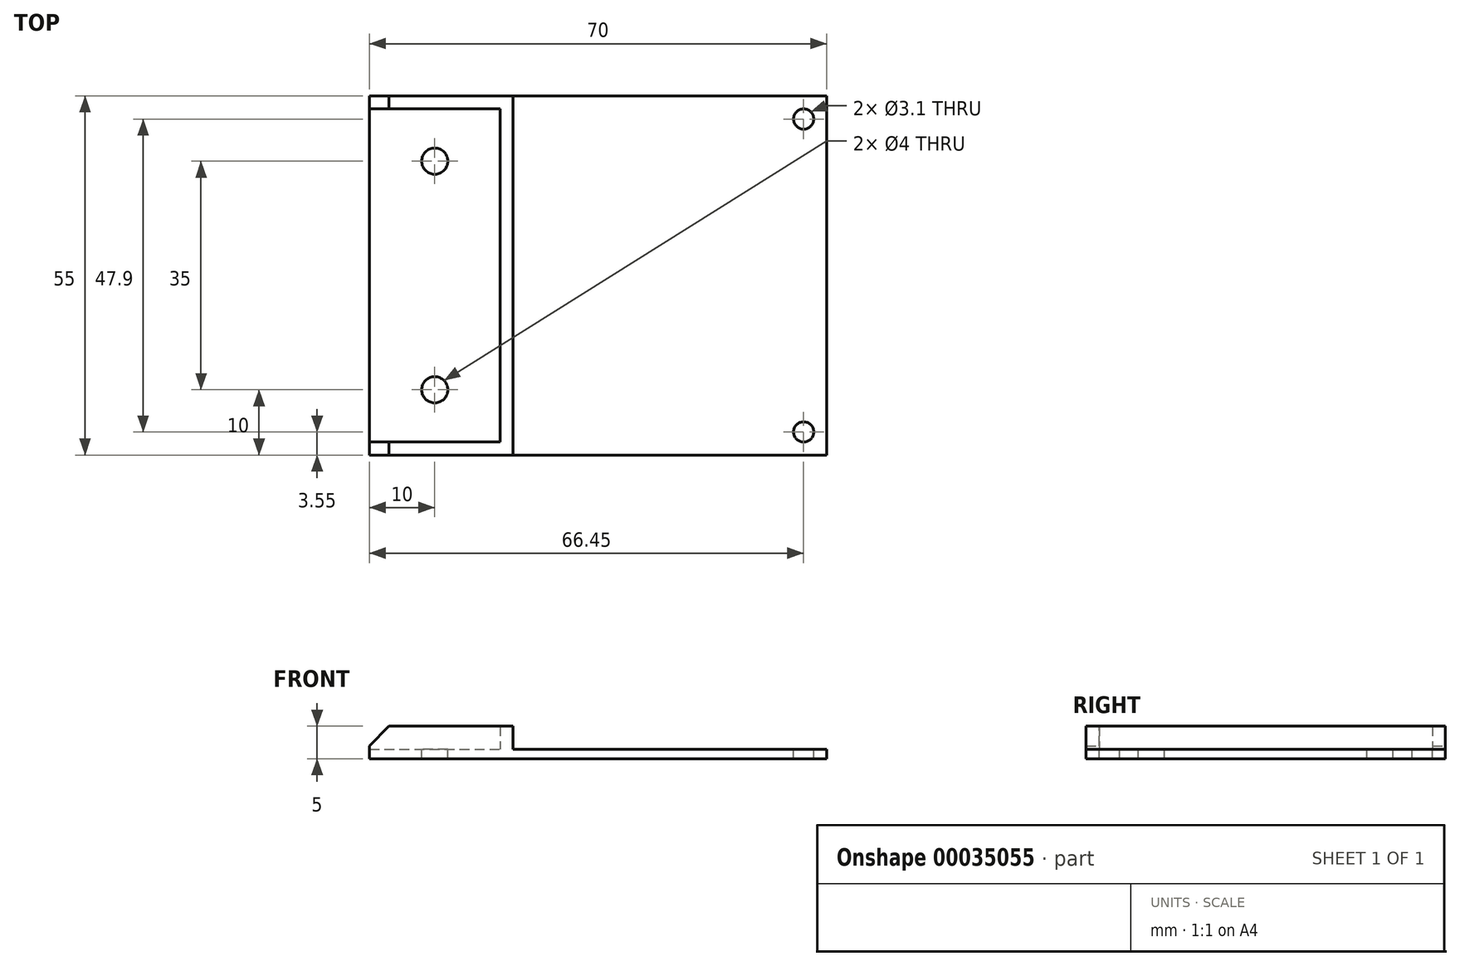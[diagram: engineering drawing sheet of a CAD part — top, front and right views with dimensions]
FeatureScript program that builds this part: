
annotation { "Feature Type Name" : "Feature", "Feature Type Description" : "" }
export const myFeature = defineFeature(function(context is Context, id is Id, definition is map)
    precondition{}
    {
        {
            var Q0;
            Q0=qCreatedBy(makeId("Top.planeOp"),FACE);
            var sketch = newSketch(context, id + "F0", { "sketchPlane" : qUnion([Q0])});
            skLineSegment(sketch, "E0.rect.bottom", {"start": v(35, -27.5) * mm, "end": v(-35, -27.5) * mm});
            skLineSegment(sketch, "E0.rect.top", {"start": v(35, 27.5) * mm, "end": v(-35, 27.5) * mm});
            skLineSegment(sketch, "E0.rect.left", {"start": v(35, -27.5) * mm, "end": v(35, 27.5) * mm});
            skLineSegment(sketch, "E0.rect.right", {"start": v(-35, -27.5) * mm, "end": v(-35, 27.5) * mm});
            skPoint(sketch, "E0.rect.middle", {"position": v(0, 0) * mm});
            skLineSegment(sketch, "E1", {"start": v(-25, 27.5) * mm, "end": v(-25, -27.5) * mm, "construction": true});
            skLineSegment(sketch, "E2", {"start": v(-35, 0) * mm, "end": v(35, 0) * mm, "construction": true});
            skLineSegment(sketch, "E3", {"start": v(35, 25.5) * mm, "end": v(-35, 25.5) * mm, "construction": true});
            skLineSegment(sketch, "E4", {"start": v(33, 27.5) * mm, "end": v(33, -27.5) * mm, "construction": true});
            skCircle(sketch, "E5", {"center": v(31.45, 23.95) * mm, "radius": 1.55 * mm});
            skCircle(sketch, "E6", {"center": v(-25, 17.5) * mm, "radius": 2 * mm});
            skCircle(sketch, "E7.MirrorC", {"center": v(-25, -17.5) * mm, "radius": 2 * mm});
            skCircle(sketch, "E8.MirrorC", {"center": v(31.45, -23.95) * mm, "radius": 1.55 * mm});
            skSolve(sketch);
        }
        {
            var Q0;
            Q0=makeQuery(id+"F0.imprint","IMPRINT",FACE,{"disambiguationData":[TD([[makeQuery(id+"F0.imprint","IMPRINT",EDGE,{"derivedFrom":sQuery(id+"F0.wireOp",EDGE,"E0.rect.bottom")}),-1.0]])]});
            extrude(context, id + "F1", {"entities" : qUnion([Q0]), "oppositeDirection" : true, "depth" : 1.5 * mm});
        }
        {
            var Q0;
            Q0=makeQuery(id+"F1.opExtrude","CAP_FACE",FACE,{"disambiguationData":[OSD([sQuery(id+"F0.wireOp",EDGE,"E0.rect.bottom"),sQuery(id+"F0.wireOp",EDGE,"E0.rect.top"),sQuery(id+"F0.wireOp",EDGE,"E0.rect.left"),sQuery(id+"F0.wireOp",EDGE,"E0.rect.right"),sQuery(id+"F0.wireOp",EDGE,"E5"),sQuery(id+"F0.wireOp",EDGE,"E6"),sQuery(id+"F0.wireOp",EDGE,"E7.MirrorC"),sQuery(id+"F0.wireOp",EDGE,"E8.MirrorC")])],"isStart":true});
            var sketch = newSketch(context, id + "F2", { "sketchPlane" : qUnion([Q0])});
            skLineSegment(sketch, "E9.top", {"start": v(-13, -25.5) * mm, "end": v(33, -25.5) * mm});
            skLineSegment(sketch, "E9.left", {"start": v(-13, 25.5) * mm, "end": v(-13, -25.5) * mm});
            skLineSegment(sketch, "E9.right", {"start": v(33, 26.5) * mm, "end": v(33, -25.5) * mm});
            skLineSegment(sketch, "E10.bottom", {"start": v(35, -27.5) * mm, "end": v(-15, -27.5) * mm});
            skLineSegment(sketch, "E10.top", {"start": v(35, 27.5) * mm, "end": v(-15, 27.5) * mm});
            skLineSegment(sketch, "E10.left", {"start": v(35, -27.5) * mm, "end": v(35, 27.5) * mm});
            skLineSegment(sketch, "E10.right", {"start": v(-15, -27.5) * mm, "end": v(-15, 27.5) * mm});
            skLineSegment(sketch, "E11.bottom", {"start": v(-35, 27.5) * mm, "end": v(-13, 27.5) * mm});
            skLineSegment(sketch, "E11.left", {"start": v(-35, 27.5) * mm, "end": v(-35, 25.5) * mm});
            skLineSegment(sketch, "E11.right", {"start": v(-13, 27.5) * mm, "end": v(-13, 25.5) * mm});
            skLineSegment(sketch, "E12.bottom", {"start": v(-13, -25.5) * mm, "end": v(-35, -25.5) * mm});
            skLineSegment(sketch, "E12.top", {"start": v(-13, -27.5) * mm, "end": v(-35, -27.5) * mm});
            skLineSegment(sketch, "E12.left", {"start": v(-13, -25.5) * mm, "end": v(-13, -27.5) * mm});
            skLineSegment(sketch, "E12.right", {"start": v(-35, -25.5) * mm, "end": v(-35, -27.5) * mm});
            skLineSegment(sketch, "E13", {"start": v(-35, 25.5) * mm, "end": v(33, 25.5) * mm});
            skSolve(sketch);
        }
        {
            var Q0;
            {var subQ3=sQuery(id+"F2.wireOp",EDGE,"E9.left");Q0=makeQuery(id+"F2.imprint","IMPRINT",FACE,{"disambiguationData":[TD([[makeQuery(id+"F2.imprint","IMPRINT",EDGE,{"derivedFrom":subQ3}),-1.0]])]});}
            var Q1;
            Q1=makeQuery(id+"F2.imprint","IMPRINT",FACE,{"disambiguationData":[TD([[makeQuery(id+"F2.imprint","IMPRINT",EDGE,{"derivedFrom":sQuery(id+"F2.wireOp",EDGE,"E10.bottom")}),-1.0]])]});
            var Q2;
            {var subQ0=sQuery(id+"F2.wireOp",EDGE,"E12.left");Q2=makeQuery(id+"F2.imprint","IMPRINT",FACE,{"disambiguationData":[TD([[makeQuery(id+"F2.imprint","IMPRINT",EDGE,{"derivedFrom":subQ0}),-1.0]])]});}
            var Q3;
            {var subQ0=sQuery(id+"F2.wireOp",EDGE,"E12.right");Q3=makeQuery(id+"F2.imprint","IMPRINT",FACE,{"disambiguationData":[TD([[makeQuery(id+"F2.imprint","IMPRINT",EDGE,{"derivedFrom":subQ0}),-1.0]])]});}
            var Q4;
            {var subQ0=sQuery(id+"F2.wireOp",EDGE,"E11.right");Q4=makeQuery(id+"F2.imprint","IMPRINT",FACE,{"disambiguationData":[TD([[makeQuery(id+"F2.imprint","IMPRINT",EDGE,{"derivedFrom":subQ0}),-1.0]])]});}
            var Q5;
            {var subQ0=sQuery(id+"F2.wireOp",EDGE,"E11.left");Q5=makeQuery(id+"F2.imprint","IMPRINT",FACE,{"disambiguationData":[TD([[makeQuery(id+"F2.imprint","IMPRINT",EDGE,{"derivedFrom":subQ0}),-1.0]])]});}
            extrude(context, id + "F3", {"entities" : qUnion([Q0, Q1, Q2, Q3, Q4, Q5]), "operationType" : NewBodyOperationType.ADD, "depth" : 3.5 * mm});
        }
        {
            var Q0;
            Q0=makeQuery(id+"F3.opExtrude","CAP_EDGE",EDGE,{"disambiguationData":[OSD([sQuery(id+"F2.wireOp",EDGE,"E11.left")])],"isStart":false});
            var Q1;
            Q1=makeQuery(id+"F3.opExtrude","CAP_EDGE",EDGE,{"disambiguationData":[OSD([sQuery(id+"F2.wireOp",EDGE,"E12.right")])],"isStart":false});
            chamfer(context, id + "F4", {"entities" : qUnion([Q0, Q1]), "width" : 3 * mm, "tangentPropagation" : true});
        }
    });
